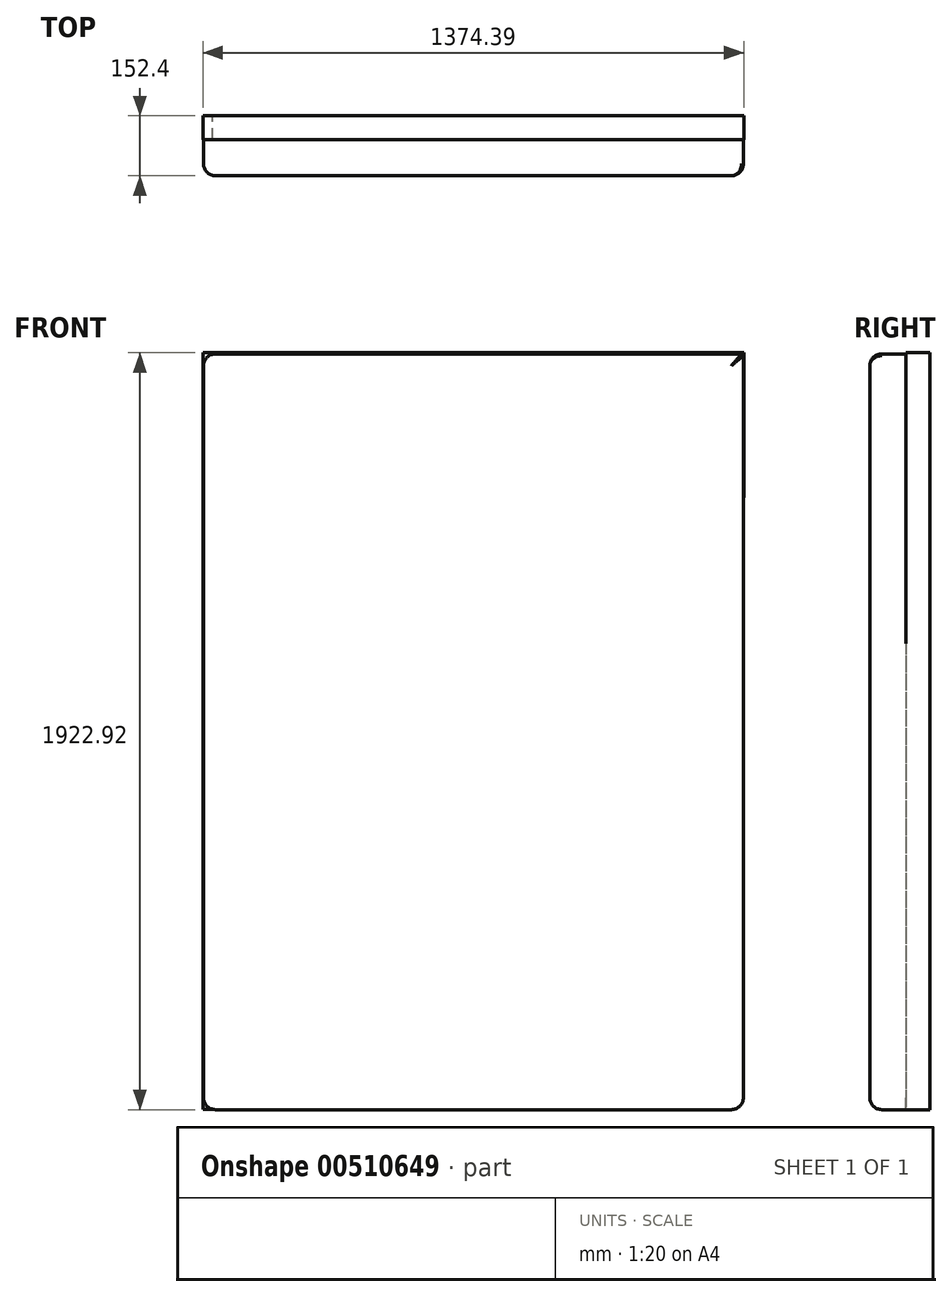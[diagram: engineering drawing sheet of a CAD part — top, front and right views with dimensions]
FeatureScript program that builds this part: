
annotation { "Feature Type Name" : "Feature", "Feature Type Description" : "" }
export const myFeature = defineFeature(function(context is Context, id is Id, definition is map)
    precondition{}
    {
        {
            var Q0;
            Q0=qCreatedBy(makeId("Front.planeOp"),FACE);
            var sketch = newSketch(context, id + "F0", { "sketchPlane" : qUnion([Q0])});
            skLineSegment(sketch, "E0", {"start": v(-636.59, 932.2) * mm, "end": v(735.01, 932.2) * mm});
            skLineSegment(sketch, "E1", {"start": v(735.01, 932.2) * mm, "end": v(735.01, -988.05) * mm});
            skLineSegment(sketch, "E2", {"start": v(735.01, -988.05) * mm, "end": v(-636.59, -988.05) * mm});
            skLineSegment(sketch, "E3", {"start": v(-636.59, -988.05) * mm, "end": v(-636.59, 932.2) * mm});
            skSolve(sketch);
        }
        {
            var Q0;
            Q0 = qSketchRegion(id + "F0", true);
            extrude(context, id + "F1", {"entities" : qUnion([Q0]), "depth" : 152.4 * mm, "offsetDistance" : 30.48 * mm});
        }
        {
            var Q0;
            Q0=makeQuery(id+"F1.opExtrude","CAP_FACE",FACE,{"disambiguationData":[OSD([sQuery(id+"F0.wireOp",EDGE,"E0"),sQuery(id+"F0.wireOp",EDGE,"E1"),sQuery(id+"F0.wireOp",EDGE,"E2"),sQuery(id+"F0.wireOp",EDGE,"E3")])],"isStart":true});
            var sketch = newSketch(context, id + "F2", { "sketchPlane" : qUnion([Q0])});
            skLineSegment(sketch, "E4", {"start": v(-735.01, 932.2) * mm, "end": v(636.59, 932.2) * mm});
            skLineSegment(sketch, "E5", {"start": v(636.59, 932.2) * mm, "end": v(636.59, -988.05) * mm});
            skLineSegment(sketch, "E6", {"start": v(636.59, -988.05) * mm, "end": v(-735.01, -988.05) * mm});
            skLineSegment(sketch, "E7", {"start": v(-735.01, -988.05) * mm, "end": v(-735.01, 932.2) * mm});
            skSolve(sketch);
        }
        {
            var Q0;
            Q0=makeQuery(id+"F2.imprint","IMPRINT",FACE,{"disambiguationData":[TD([[makeQuery(id+"F2.imprint","IMPRINT",EDGE,{"derivedFrom":sQuery(id+"F2.wireOp",EDGE,"E4")}),1.0]])]});
            var sketch = newSketch(context, id + "F3", { "sketchPlane" : qUnion([Q0])});
            skLineSegment(sketch, "E8", {"start": v(-736.4, 934.87) * mm, "end": v(637.98, 934.87) * mm});
            skLineSegment(sketch, "E9", {"start": v(637.98, 934.87) * mm, "end": v(637.98, -987.1) * mm});
            skLineSegment(sketch, "E10", {"start": v(637.98, -987.1) * mm, "end": v(-732.78, -987.1) * mm});
            skLineSegment(sketch, "E11", {"start": v(-732.78, -987.1) * mm, "end": v(-736.4, 934.87) * mm});
            skSolve(sketch);
        }
        {
            var Q0;
            Q0 = qSketchRegion(id + "F3", true);
            extrude(context, id + "F4", {"entities" : qUnion([Q0]), "operationType" : NewBodyOperationType.ADD, "oppositeDirection" : true, "depth" : 60.96 * mm, "offsetDistance" : 30.48 * mm});
        }
        {
            var Q0;
            Q0=makeQuery(id+"F1.opExtrude","CAP_EDGE",EDGE,{"disambiguationData":[OSD([sQuery(id+"F0.wireOp",EDGE,"E0")])],"isStart":false});
            var Q1;
            Q1=makeQuery(id+"F1.opExtrude","CAP_EDGE",EDGE,{"disambiguationData":[OSD([sQuery(id+"F0.wireOp",EDGE,"E1")])],"isStart":false});
            var Q2;
            Q2=makeQuery(id+"F1.opExtrude","SWEPT_EDGE",EDGE,{"disambiguationData":[OSD([sQuery(id+"F0.wireOp",EDGE,"E0"),sQuery(id+"F0.wireOp",EDGE,"E3")])]});
            var Q3;
            Q3=makeQuery(id+"F1.opExtrude","CAP_EDGE",EDGE,{"disambiguationData":[OSD([sQuery(id+"F0.wireOp",EDGE,"E3")])],"isStart":false});
            var Q4;
            Q4=makeQuery(id+"F1.opExtrude","SWEPT_EDGE",EDGE,{"disambiguationData":[OSD([sQuery(id+"F0.wireOp",EDGE,"E2"),sQuery(id+"F0.wireOp",EDGE,"E3")])]});
            var Q5;
            Q5=makeQuery(id+"F1.opExtrude","CAP_EDGE",EDGE,{"disambiguationData":[OSD([sQuery(id+"F0.wireOp",EDGE,"E2")])],"isStart":false});
            var Q6;
            Q6=makeQuery(id+"F1.opExtrude","SWEPT_EDGE",EDGE,{"disambiguationData":[OSD([sQuery(id+"F0.wireOp",EDGE,"E1"),sQuery(id+"F0.wireOp",EDGE,"E2")])]});
            fillet(context, id + "F5", {"entities" : qUnion([Q0, Q1, Q2, Q3, Q4, Q5, Q6]), "radius" : 30.48 * mm, "tangentPropagation" : true, "allowEdgeOverflow" : false});
        }
        {
            var Q0;
            Q0=makeQuery(id+"F1.opExtrude","SWEPT_EDGE",EDGE,{"disambiguationData":[OSD([sQuery(id+"F0.wireOp",EDGE,"E0"),sQuery(id+"F0.wireOp",EDGE,"E1")])]});
            fillet(context, id + "F6", {"entities" : qUnion([Q0]), "radius" : 4.57 * mm, "tangentPropagation" : true, "allowEdgeOverflow" : false});
        }
    });
